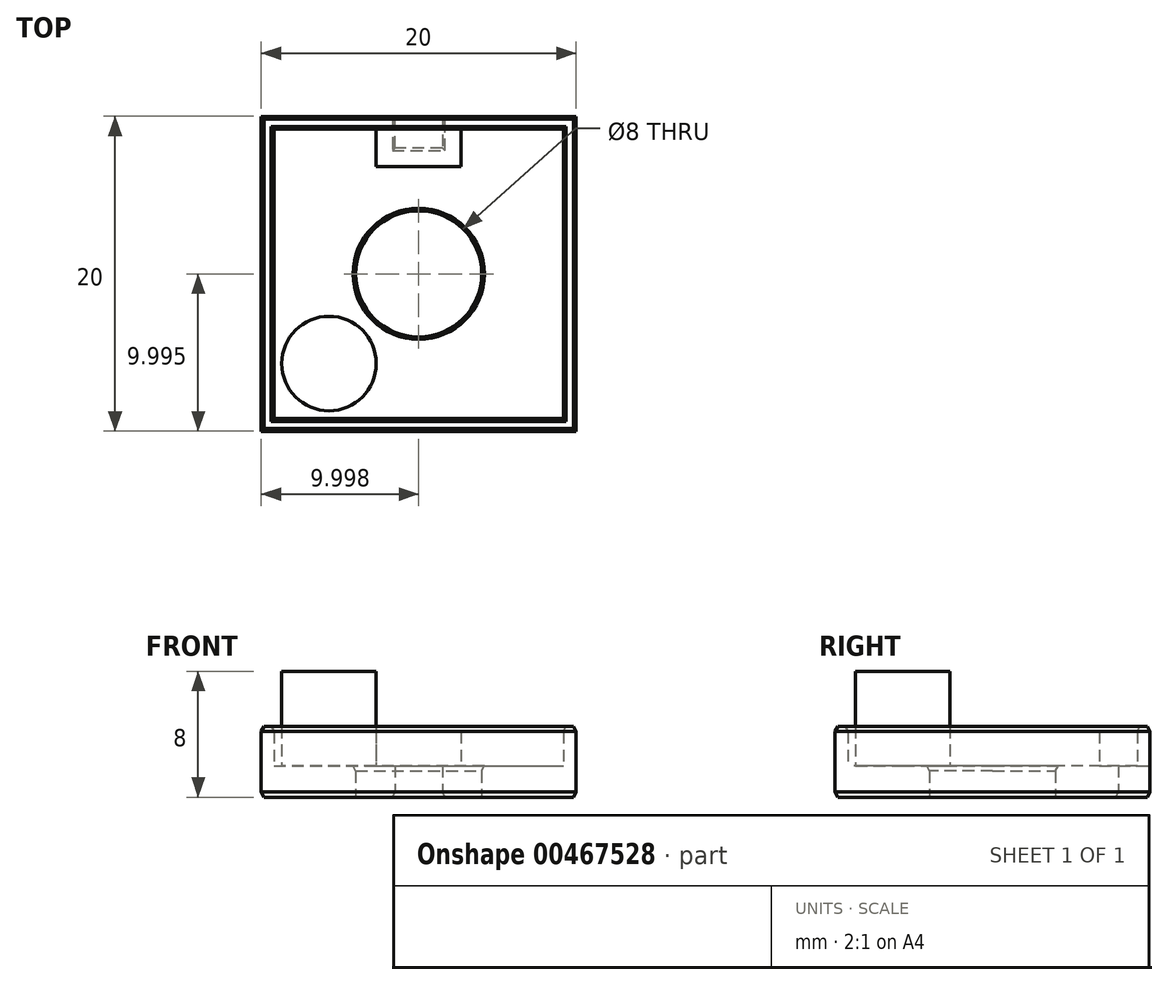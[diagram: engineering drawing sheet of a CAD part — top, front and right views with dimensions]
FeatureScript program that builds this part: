
annotation { "Feature Type Name" : "Feature", "Feature Type Description" : "" }
export const myFeature = defineFeature(function(context is Context, id is Id, definition is map)
    precondition{}
    {
        {
            var Q0;
            Q0=qCreatedBy(makeId("Top.planeOp"),FACE);
            var sketch = newSketch(context, id + "F0", { "sketchPlane" : qUnion([Q0])});
            skLineSegment(sketch, "E0.bottom", {"start": v(-6.97, 8) * mm, "end": v(13.03, 8) * mm});
            skLineSegment(sketch, "E0.top", {"start": v(-6.97, -12) * mm, "end": v(13.03, -12) * mm});
            skLineSegment(sketch, "E0.left", {"start": v(-6.97, 8) * mm, "end": v(-6.97, -12) * mm});
            skLineSegment(sketch, "E0.right", {"start": v(13.03, 8) * mm, "end": v(13.03, -12) * mm});
            skLineSegment(sketch, "E1.0", {"start": v(-6.17, 7.2) * mm, "end": v(12.23, 7.2) * mm});
            skLineSegment(sketch, "E1.1", {"start": v(-6.17, 7.2) * mm, "end": v(-6.17, -11.2) * mm});
            skLineSegment(sketch, "E1.2", {"start": v(-6.17, -11.2) * mm, "end": v(12.23, -11.2) * mm});
            skLineSegment(sketch, "E1.3", {"start": v(12.23, 7.2) * mm, "end": v(12.23, -11.2) * mm});
            skSolve(sketch);
        }
        {
            var Q0;
            Q0=makeQuery(id+"F0.imprint","IMPRINT",FACE,{"disambiguationData":[TD([[makeQuery(id+"F0.imprint","IMPRINT",EDGE,{"derivedFrom":sQuery(id+"F0.wireOp",EDGE,"E1.0")}),-1.0]])]});
            var Q1;
            Q1=makeQuery(id+"F0.imprint","IMPRINT",FACE,{"disambiguationData":[TD([[makeQuery(id+"F0.imprint","IMPRINT",EDGE,{"derivedFrom":sQuery(id+"F0.wireOp",EDGE,"E0.bottom")}),-1.0]])]});
            extrude(context, id + "F1", {"entities" : qUnion([Q0, Q1]), "oppositeDirection" : true, "depth" : 2 * mm});
        }
        {
            var Q0;
            Q0=makeQuery(id+"F0.imprint","IMPRINT",FACE,{"disambiguationData":[TD([[makeQuery(id+"F0.imprint","IMPRINT",EDGE,{"derivedFrom":sQuery(id+"F0.wireOp",EDGE,"E0.bottom")}),-1.0]])]});
            extrude(context, id + "F2", {"entities" : qUnion([Q0]), "operationType" : NewBodyOperationType.ADD, "depth" : 2.5 * mm});
        }
        {
            var Q0;
            Q0=makeQuery(id+"F1.opExtrude","CAP_FACE",FACE,{"disambiguationData":[OSD([sQuery(id+"F0.wireOp",EDGE,"E0.bottom"),sQuery(id+"F0.wireOp",EDGE,"E0.top"),sQuery(id+"F0.wireOp",EDGE,"E0.left"),sQuery(id+"F0.wireOp",EDGE,"E0.right")])],"isStart":false});
            var sketch = newSketch(context, id + "F3", { "sketchPlane" : qUnion([Q0])});
            skLineSegment(sketch, "E2", {"start": v(3.03, -6) * mm, "end": v(1.53, -6) * mm});
            skLineSegment(sketch, "E3", {"start": v(1.53, -6) * mm, "end": v(1.53, -8) * mm});
            skLineSegment(sketch, "E4", {"start": v(3.03, -6) * mm, "end": v(4.53, -6) * mm});
            skLineSegment(sketch, "E5", {"start": v(4.53, -6) * mm, "end": v(4.53, -8) * mm});
            skPoint(sketch, "E6.start.orphan", {"position": v(3.03, -8) * mm});
            skSolve(sketch);
        }
        {
            var Q0;
            Q0=makeQuery(id+"F3.imprint","IMPRINT",FACE,{"disambiguationData":[TD([[makeQuery(id+"F3.imprint","IMPRINT",EDGE,{"derivedFrom":sQuery(id+"F3.wireOp",EDGE,"E2")}),1.0]])]});
            extrude(context, id + "F4", {"entities" : qUnion([Q0]), "operationType" : NewBodyOperationType.REMOVE, "oppositeDirection" : true, "depth" : 2 * mm});
        }
        {
            var Q0;
            Q0=makeQuery(id+"F1.opExtrude","CAP_FACE",FACE,{"disambiguationData":[OSD([sQuery(id+"F0.wireOp",EDGE,"E0.bottom"),sQuery(id+"F0.wireOp",EDGE,"E0.top"),sQuery(id+"F0.wireOp",EDGE,"E0.left"),sQuery(id+"F0.wireOp",EDGE,"E0.right")])],"isStart":false});
            chamfer(context, id + "F5", {"entities" : qUnion([Q0]), "chamferType" : ChamferType.TWO_OFFSETS, "width1" : .167 * mm, "oppositeDirection" : true, "width2" : .334 * mm, "tangentPropagation" : true});
        }
        {
            var Q0;
            Q0=makeQuery(id+"F1.opExtrude","CAP_FACE",FACE,{"disambiguationData":[OSD([sQuery(id+"F0.wireOp",EDGE,"E0.bottom"),sQuery(id+"F0.wireOp",EDGE,"E0.top"),sQuery(id+"F0.wireOp",EDGE,"E0.left"),sQuery(id+"F0.wireOp",EDGE,"E0.right")])],"isStart":false});
            var sketch = newSketch(context, id + "F6", { "sketchPlane" : qUnion([Q0])});
            skCircle(sketch, "E7", {"center": v(3.03, 2) * mm, "radius": 4 * mm});
            skPoint(sketch, "E8.start.orphan", {"position": v(12.86, 11.84) * mm});
            skPoint(sketch, "E9.trimOffspring.end.orphan", {"position": v(-6.8, -7.83) * mm});
            skSolve(sketch);
        }
        {
            var Q0;
            Q0=makeQuery(id+"F6.imprint","IMPRINT",FACE,{"disambiguationData":[TD([[makeQuery(id+"F6.imprint","IMPRINT",EDGE,{"derivedFrom":sQuery(id+"F6.wireOp",EDGE,"E7")}),1.0]])]});
            extrude(context, id + "F7", {"entities" : qUnion([Q0]), "operationType" : NewBodyOperationType.REMOVE, "endBound" : BoundingType.THROUGH_ALL, "oppositeDirection" : true, "depth" : 25 * mm});
        }
        {
            var Q0;
            Q0=makeQuery(id+"F7.boolean.opBoolean","COPY",EDGE,{"derivedFrom":makeQuery(id+"F7.opExtrude","CAP_EDGE",EDGE,{"disambiguationData":[OSD([sQuery(id+"F6.wireOp",EDGE,"E7")])],"isStart":true})});
            var Q1;
            Q1=makeQuery(id+"F7.boolean.opBoolean","INTERSECT",EDGE,{"derivedFrom":[makeQuery(id+"F1.opExtrude","CAP_FACE",FACE,{"disambiguationData":[OSD([sQuery(id+"F0.wireOp",EDGE,"E0.bottom"),sQuery(id+"F0.wireOp",EDGE,"E0.top"),sQuery(id+"F0.wireOp",EDGE,"E0.left"),sQuery(id+"F0.wireOp",EDGE,"E0.right")])],"isStart":true}),makeQuery(id+"F7.opExtrude","SWEPT_FACE",FACE,{"disambiguationData":[OSD([sQuery(id+"F6.wireOp",EDGE,"E7")])]})]});
            chamfer(context, id + "F8", {"entities" : qUnion([Q0, Q1]), "chamferType" : ChamferType.TWO_OFFSETS, "width1" : .167 * mm, "oppositeDirection" : true, "width2" : .334 * mm, "tangentPropagation" : true});
        }
        {
            var Q0;
            Q0=makeQuery(id+"F2.opExtrude","CAP_FACE",FACE,{"disambiguationData":[OSD([sQuery(id+"F0.wireOp",EDGE,"E0.bottom"),sQuery(id+"F0.wireOp",EDGE,"E0.top"),sQuery(id+"F0.wireOp",EDGE,"E0.left"),sQuery(id+"F0.wireOp",EDGE,"E0.right"),sQuery(id+"F0.wireOp",EDGE,"E1.0"),sQuery(id+"F0.wireOp",EDGE,"E1.1"),sQuery(id+"F0.wireOp",EDGE,"E1.2"),sQuery(id+"F0.wireOp",EDGE,"E1.3")])],"isStart":false});
            chamfer(context, id + "F9", {"entities" : qUnion([Q0]), "chamferType" : ChamferType.TWO_OFFSETS, "width1" : .334 * mm, "oppositeDirection" : false, "width2" : .167 * mm, "tangentPropagation" : true});
        }
        {
            var Q0;
            Q0=makeQuery(id+"F0.imprint","IMPRINT",FACE,{"disambiguationData":[TD([[makeQuery(id+"F0.imprint","IMPRINT",EDGE,{"derivedFrom":sQuery(id+"F0.wireOp",EDGE,"E1.0")}),-1.0]])]});
            var sketch = newSketch(context, id + "F10", { "sketchPlane" : qUnion([Q0])});
            skLineSegment(sketch, "E10.0", {"start": v(1.53, 6) * mm, "end": v(4.53, 6) * mm});
            skPoint(sketch, "E11.0", {"position": v(4.53, 6.6) * mm});
            skLineSegment(sketch, "E12.0", {"start": v(1.53, 6) * mm, "end": v(1.53, 7.2) * mm});
            skLineSegment(sketch, "E13.0", {"start": v(4.53, 6) * mm, "end": v(4.53, 7.2) * mm});
            skLineSegment(sketch, "E14.0", {"start": v(0.33, 4.8) * mm, "end": v(0.33, 7.2) * mm});
            skLineSegment(sketch, "E14.1", {"start": v(0.33, 4.8) * mm, "end": v(5.73, 4.8) * mm});
            skLineSegment(sketch, "E14.2", {"start": v(5.73, 4.8) * mm, "end": v(5.73, 7.2) * mm});
            skLineSegment(sketch, "E15", {"start": v(0.33, 7.2) * mm, "end": v(5.73, 7.2) * mm});
            skSolve(sketch);
        }
        {
            var Q0;
            Q0=makeQuery(id+"F10.imprint","IMPRINT",FACE,{"disambiguationData":[TD([[makeQuery(id+"F10.imprint","IMPRINT",EDGE,{"derivedFrom":sQuery(id+"F10.wireOp",EDGE,"E10.0")}),-1.0]])]});
            var Q1;
            Q1=makeQuery(id+"F10.imprint","IMPRINT",FACE,{"disambiguationData":[TD([[makeQuery(id+"F10.imprint","IMPRINT",EDGE,{"derivedFrom":sQuery(id+"F10.wireOp",EDGE,"E10.0")}),1.0]])]});
            extrude(context, id + "F11", {"entities" : qUnion([Q0, Q1]), "operationType" : NewBodyOperationType.ADD, "depth" : 2.17 * mm, "offsetDistance" : 25 * mm});
        }
        {
            var Q0;
            Q0=makeQuery(id+"F0.imprint","IMPRINT",FACE,{"disambiguationData":[TD([[makeQuery(id+"F0.imprint","IMPRINT",EDGE,{"derivedFrom":sQuery(id+"F0.wireOp",EDGE,"E1.0")}),-1.0]])]});
            var sketch = newSketch(context, id + "F12", { "sketchPlane" : qUnion([Q0])});
            skLineSegment(sketch, "E16.0.0", {"start": v(12.23, -11.2) * mm, "end": v(12.23, 7.2) * mm});
            skLineSegment(sketch, "E16.0.1", {"start": v(12.23, 7.2) * mm, "end": v(-6.17, 7.2) * mm});
            skLineSegment(sketch, "E16.0.2", {"start": v(-6.17, 7.2) * mm, "end": v(-6.17, -11.2) * mm});
            skLineSegment(sketch, "E16.0.3", {"start": v(-6.17, -11.2) * mm, "end": v(12.23, -11.2) * mm});
            skCircle(sketch, "E17", {"center": v(-2.67, -7.7) * mm, "radius": 3 * mm});
            skSolve(sketch);
        }
        {
            var Q0;
            Q0=makeQuery(id+"F12.imprint","IMPRINT",FACE,{"disambiguationData":[TD([[makeQuery(id+"F12.imprint","IMPRINT",EDGE,{"derivedFrom":sQuery(id+"F12.wireOp",EDGE,"E17")}),1.0]])]});
            var Q1;
            Q1=sQuery(id+"F12.wireOp",EDGE,"E17");
            extrude(context, id + "F13", {"entities" : qUnion([Q0]), "operationType" : NewBodyOperationType.ADD, "surfaceEntities" : qUnion([Q1]), "depth" : 6 * mm, "offsetDistance" : 25 * mm});
        }
    });
